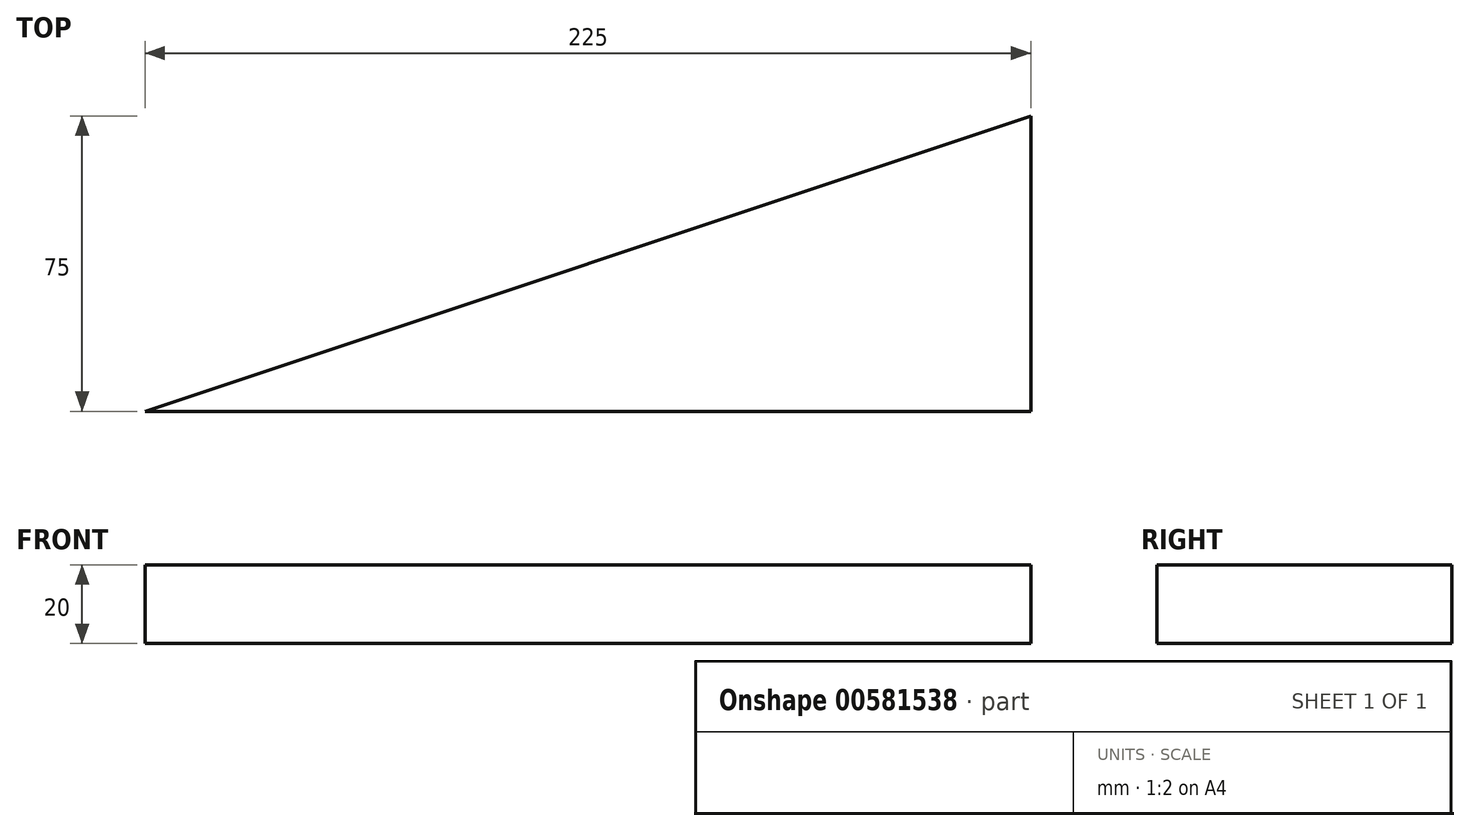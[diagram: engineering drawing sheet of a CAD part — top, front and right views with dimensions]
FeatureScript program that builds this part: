
annotation { "Feature Type Name" : "Feature", "Feature Type Description" : "" }
export const myFeature = defineFeature(function(context is Context, id is Id, definition is map)
    precondition{}
    {
        {
            var Q0;
            Q0=qCreatedBy(makeId("Top.planeOp"),FACE);
            var sketch = newSketch(context, id + "F0", { "sketchPlane" : qUnion([Q0])});
            skLineSegment(sketch, "E0", {"start": v(0, 0) * mm, "end": v(225, 75) * mm});
            skLineSegment(sketch, "E1", {"start": v(225, 75) * mm, "end": v(225, 0) * mm});
            skLineSegment(sketch, "E2", {"start": v(225, 0) * mm, "end": v(0, 0) * mm});
            skSolve(sketch);
        }
        {
            var Q0;
            Q0 = qSketchRegion(id + "F0", true);
            extrude(context, id + "F1", {"entities" : qUnion([Q0]), "depth" : 20 * mm, "offsetDistance" : 25 * mm});
        }
    });
